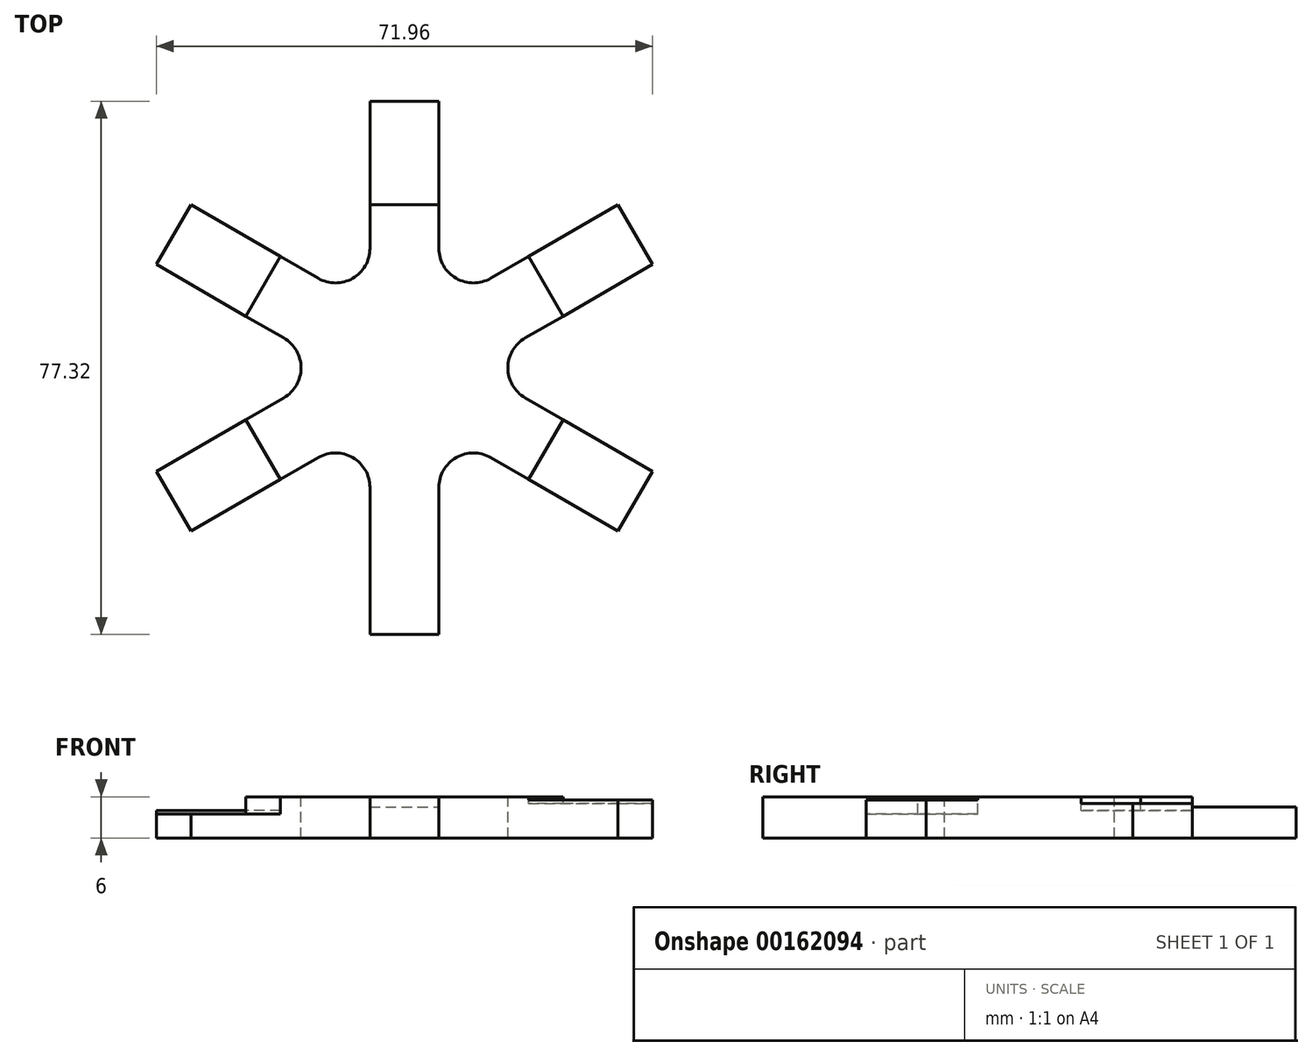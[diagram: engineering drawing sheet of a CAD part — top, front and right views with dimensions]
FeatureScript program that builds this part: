
annotation { "Feature Type Name" : "Feature", "Feature Type Description" : "" }
export const myFeature = defineFeature(function(context is Context, id is Id, definition is map)
    precondition{}
    {
        {
            var Q0;
            Q0=qCreatedBy(makeId("Top.planeOp"),FACE);
            var sketch = newSketch(context, id + "F0", { "sketchPlane" : qUnion([Q0])});
            skLineSegment(sketch, "E0", {"start": v(-5, 38.66) * mm, "end": v(5, 38.66) * mm});
            skLineSegment(sketch, "E1", {"start": v(5, 38.66) * mm, "end": v(5, 8.66) * mm});
            skLineSegment(sketch, "E2", {"start": v(5, 8.66) * mm, "end": v(30.98, 23.66) * mm});
            skLineSegment(sketch, "E3", {"start": v(30.98, 23.66) * mm, "end": v(35.98, 15) * mm});
            skLineSegment(sketch, "E4", {"start": v(35.98, 15) * mm, "end": v(10, 0) * mm});
            skLineSegment(sketch, "E5", {"start": v(10, 0) * mm, "end": v(35.98, -15) * mm});
            skLineSegment(sketch, "E6", {"start": v(35.98, -15) * mm, "end": v(30.98, -23.66) * mm});
            skLineSegment(sketch, "E7", {"start": v(30.98, -23.66) * mm, "end": v(5, -8.66) * mm});
            skLineSegment(sketch, "E8", {"start": v(5, -8.66) * mm, "end": v(5, -38.66) * mm});
            skLineSegment(sketch, "E9", {"start": v(5, -38.66) * mm, "end": v(-5, -38.66) * mm});
            skLineSegment(sketch, "E10", {"start": v(-5, -38.66) * mm, "end": v(-5, -8.66) * mm});
            skLineSegment(sketch, "E11", {"start": v(-5, -8.66) * mm, "end": v(-30.98, -23.66) * mm});
            skLineSegment(sketch, "E12", {"start": v(-30.98, -23.66) * mm, "end": v(-35.98, -15) * mm});
            skLineSegment(sketch, "E13", {"start": v(-35.98, -15) * mm, "end": v(-10, 0) * mm});
            skLineSegment(sketch, "E14", {"start": v(-10, 0) * mm, "end": v(-35.98, 15) * mm});
            skLineSegment(sketch, "E15", {"start": v(-35.98, 15) * mm, "end": v(-30.98, 23.66) * mm});
            skLineSegment(sketch, "E16", {"start": v(-30.98, 23.66) * mm, "end": v(-5, 8.66) * mm});
            skLineSegment(sketch, "E17", {"start": v(-5, 38.66) * mm, "end": v(-5, 8.66) * mm});
            skLineSegment(sketch, "E18", {"start": v(0, 0) * mm, "end": v(0, 37.36) * mm, "construction": true});
            skLineSegment(sketch, "E19", {"start": v(0, 0) * mm, "end": v(-33.94, 19.6) * mm, "construction": true});
            skLineSegment(sketch, "E20", {"start": v(0, 0) * mm, "end": v(-35.55, -20.52) * mm, "construction": true});
            skLineSegment(sketch, "E21", {"start": v(0, 0) * mm, "end": v(0, -31.61) * mm, "construction": true});
            skLineSegment(sketch, "E22", {"start": v(0, 0) * mm, "end": v(26.79, -15.47) * mm, "construction": true});
            skLineSegment(sketch, "E23", {"start": v(0, 0) * mm, "end": v(38.43, 22.19) * mm, "construction": true});
            skSolve(sketch);
        }
        {
            var Q0;
            Q0=makeQuery(id+"F0.imprint","IMPRINT",FACE,{"disambiguationData":[TD([[makeQuery(id+"F0.imprint","IMPRINT",EDGE,{"derivedFrom":sQuery(id+"F0.wireOp",EDGE,"E0")}),-1.0]])]});
            extrude(context, id + "F1", {"entities" : qUnion([Q0]), "depth" : 6 * mm});
        }
        {
            var Q0;
            Q0=makeQuery(id+"F1.opExtrude","SWEPT_EDGE",EDGE,{"disambiguationData":[OSD([sQuery(id+"F0.wireOp",EDGE,"E16"),sQuery(id+"F0.wireOp",EDGE,"E17")])]});
            var Q1;
            Q1=makeQuery(id+"F1.opExtrude","SWEPT_EDGE",EDGE,{"disambiguationData":[OSD([sQuery(id+"F0.wireOp",EDGE,"E1"),sQuery(id+"F0.wireOp",EDGE,"E2")])]});
            var Q2;
            Q2=makeQuery(id+"F1.opExtrude","SWEPT_EDGE",EDGE,{"disambiguationData":[OSD([sQuery(id+"F0.wireOp",EDGE,"E4"),sQuery(id+"F0.wireOp",EDGE,"E5")])]});
            var Q3;
            Q3=makeQuery(id+"F1.opExtrude","SWEPT_EDGE",EDGE,{"disambiguationData":[OSD([sQuery(id+"F0.wireOp",EDGE,"E7"),sQuery(id+"F0.wireOp",EDGE,"E8")])]});
            var Q4;
            Q4=makeQuery(id+"F1.opExtrude","SWEPT_EDGE",EDGE,{"disambiguationData":[OSD([sQuery(id+"F0.wireOp",EDGE,"E10"),sQuery(id+"F0.wireOp",EDGE,"E11")])]});
            var Q5;
            Q5=makeQuery(id+"F1.opExtrude","SWEPT_EDGE",EDGE,{"disambiguationData":[OSD([sQuery(id+"F0.wireOp",EDGE,"E13"),sQuery(id+"F0.wireOp",EDGE,"E14")])]});
            fillet(context, id + "F2", {"entities" : qUnion([Q0, Q1, Q2, Q3, Q4, Q5]), "radius" : 5 * mm, "tangentPropagation" : true, "allowEdgeOverflow" : false});
        }
        {
            var Q0;
            Q0=makeQuery(id+"F1.opExtrude","CAP_FACE",FACE,{"disambiguationData":[OSD([sQuery(id+"F0.wireOp",EDGE,"E0"),sQuery(id+"F0.wireOp",EDGE,"E1"),sQuery(id+"F0.wireOp",EDGE,"E2"),sQuery(id+"F0.wireOp",EDGE,"E3"),sQuery(id+"F0.wireOp",EDGE,"E4"),sQuery(id+"F0.wireOp",EDGE,"E5"),sQuery(id+"F0.wireOp",EDGE,"E6"),sQuery(id+"F0.wireOp",EDGE,"E7"),sQuery(id+"F0.wireOp",EDGE,"E8"),sQuery(id+"F0.wireOp",EDGE,"E9"),sQuery(id+"F0.wireOp",EDGE,"E10"),sQuery(id+"F0.wireOp",EDGE,"E11"),sQuery(id+"F0.wireOp",EDGE,"E12"),sQuery(id+"F0.wireOp",EDGE,"E13"),sQuery(id+"F0.wireOp",EDGE,"E14"),sQuery(id+"F0.wireOp",EDGE,"E15"),sQuery(id+"F0.wireOp",EDGE,"E16"),sQuery(id+"F0.wireOp",EDGE,"E17")])],"isStart":false});
            var sketch = newSketch(context, id + "F3", { "sketchPlane" : qUnion([Q0])});
            skLineSegment(sketch, "E24", {"start": v(-30.98, -23.66) * mm, "end": v(-35.98, -15) * mm});
            skLineSegment(sketch, "E25", {"start": v(-35.98, -15) * mm, "end": v(-23, -7.5) * mm});
            skPoint(sketch, "E26.endSnap0", {"position": v(-21.74, -18.33) * mm});
            skLineSegment(sketch, "E27", {"start": v(-23, -7.5) * mm, "end": v(-18, -16.16) * mm});
            skLineSegment(sketch, "E28", {"start": v(-18, -16.16) * mm, "end": v(-30.98, -23.66) * mm});
            skLineSegment(sketch, "E29", {"start": v(-35.98, 15) * mm, "end": v(-30.98, 23.66) * mm});
            skLineSegment(sketch, "E30", {"start": v(-30.98, 23.66) * mm, "end": v(-18, 16.16) * mm});
            skLineSegment(sketch, "E31", {"start": v(-18, 16.16) * mm, "end": v(-23, 7.5) * mm});
            skLineSegment(sketch, "E32", {"start": v(-23, 7.5) * mm, "end": v(-35.98, 15) * mm});
            skLineSegment(sketch, "E33", {"start": v(-5, 38.66) * mm, "end": v(5, 38.66) * mm});
            skLineSegment(sketch, "E34", {"start": v(5, 38.66) * mm, "end": v(5, 23.66) * mm});
            skLineSegment(sketch, "E35", {"start": v(5, 23.66) * mm, "end": v(-5, 23.66) * mm});
            skLineSegment(sketch, "E36", {"start": v(-5, 23.66) * mm, "end": v(-5, 38.66) * mm});
            skLineSegment(sketch, "E37", {"start": v(30.98, 23.66) * mm, "end": v(35.98, 15) * mm});
            skLineSegment(sketch, "E38", {"start": v(35.98, 15) * mm, "end": v(23, 7.5) * mm});
            skLineSegment(sketch, "E39", {"start": v(23, 7.5) * mm, "end": v(18, 16.16) * mm});
            skLineSegment(sketch, "E40", {"start": v(18, 16.16) * mm, "end": v(30.98, 23.66) * mm});
            skLineSegment(sketch, "E41", {"start": v(35.98, -15) * mm, "end": v(30.98, -23.66) * mm});
            skLineSegment(sketch, "E42", {"start": v(30.98, -23.66) * mm, "end": v(18, -16.16) * mm});
            skLineSegment(sketch, "E43", {"start": v(18, -16.16) * mm, "end": v(23, -7.5) * mm});
            skLineSegment(sketch, "E44", {"start": v(23, -7.5) * mm, "end": v(35.98, -15) * mm});
            skSolve(sketch);
        }
        {
            var Q0;
            Q0=makeQuery(id+"F3.imprint","IMPRINT",FACE,{"disambiguationData":[TD([[makeQuery(id+"F3.imprint","IMPRINT",EDGE,{"derivedFrom":sQuery(id+"F3.wireOp",EDGE,"E24")}),-1.0]])]});
            extrude(context, id + "F4", {"entities" : qUnion([Q0]), "operationType" : NewBodyOperationType.REMOVE, "oppositeDirection" : true, "depth" : 2.5 * mm});
        }
        {
            var Q0;
            Q0=makeQuery(id+"F3.imprint","IMPRINT",FACE,{"disambiguationData":[TD([[makeQuery(id+"F3.imprint","IMPRINT",EDGE,{"derivedFrom":sQuery(id+"F3.wireOp",EDGE,"E29")}),-1.0]])]});
            extrude(context, id + "F5", {"entities" : qUnion([Q0]), "operationType" : NewBodyOperationType.REMOVE, "oppositeDirection" : true, "depth" : 2 * mm});
        }
        {
            var Q0;
            Q0=makeQuery(id+"F3.imprint","IMPRINT",FACE,{"disambiguationData":[TD([[makeQuery(id+"F3.imprint","IMPRINT",EDGE,{"derivedFrom":sQuery(id+"F3.wireOp",EDGE,"E33")}),-1.0]])]});
            extrude(context, id + "F6", {"entities" : qUnion([Q0]), "operationType" : NewBodyOperationType.REMOVE, "oppositeDirection" : true, "depth" : 1.5 * mm});
        }
        {
            var Q0;
            Q0=makeQuery(id+"F3.imprint","IMPRINT",FACE,{"disambiguationData":[TD([[makeQuery(id+"F3.imprint","IMPRINT",EDGE,{"derivedFrom":sQuery(id+"F3.wireOp",EDGE,"E37")}),-1.0]])]});
            extrude(context, id + "F7", {"entities" : qUnion([Q0]), "operationType" : NewBodyOperationType.REMOVE, "oppositeDirection" : true, "depth" : 1 * mm});
        }
        {
            var Q0;
            Q0=makeQuery(id+"F3.imprint","IMPRINT",FACE,{"disambiguationData":[TD([[makeQuery(id+"F3.imprint","IMPRINT",EDGE,{"derivedFrom":sQuery(id+"F3.wireOp",EDGE,"E41")}),-1.0]])]});
            extrude(context, id + "F8", {"entities" : qUnion([Q0]), "operationType" : NewBodyOperationType.REMOVE, "oppositeDirection" : true, "depth" : 0.5 * mm});
        }
    });
